FCSTD DOCUMENT  (FreeCAD 1.2R20251216 (Git shallow))
Label: gripper-assembly
License: All rights reserved
LicenseURL: https://en.wikipedia.org/wiki/All_rights_reserved
objects: App::FeaturePython×38, App::Link×31, App::DocumentObjectGroup×2, App::Point×1, Assembly::JointGroup×1, Assembly::AssemblyObject×1
EXTERNAL_REF file=gripper-parts.FCStd obj=Body077
EXTERNAL_REF file=gripper-parts.FCStd obj=Body076
EXTERNAL_REF file=gripper-parts.FCStd obj=Part__Mirroring004
EXTERNAL_REF file=gripper-parts.FCStd obj=Body059
EXTERNAL_REF file=gripper-parts.FCStd obj=Body058
EXTERNAL_REF file=gripper-parts.FCStd obj=Body057
EXTERNAL_REF file=gripper-parts.FCStd obj=Body056
EXTERNAL_REF file=gripper-parts.FCStd obj=Body055
EXTERNAL_REF file=gripper-parts.FCStd obj=Body054
EXTERNAL_REF file=gripper-parts.FCStd obj=Part015
EXTERNAL_REF file=gripper-parts.FCStd obj=Body050
EXTERNAL_REF file=gripper-parts.FCStd obj=Body044
EXTERNAL_REF file=gripper-parts.FCStd obj=Part__Mirroring
EXTERNAL_REF file=gripper-parts.FCStd obj=Body051
EXTERNAL_REF file=gripper-parts.FCStd obj=Body052
EXTERNAL_REF file=gripper-parts.FCStd obj=Body
EXTERNAL_REF file=gripper-parts.FCStd obj=Solid
EXTERNAL_REF file=gripper-parts.FCStd obj=Body002
EXTERNAL_REF file=gripper-parts.FCStd obj=Part__Mirroring003
EXTERNAL_REF file=gripper-parts.FCStd obj=Part__Mirroring002
EXTERNAL_REF file=gripper-parts.FCStd obj=Part__Mirroring005
EXTERNAL_REF file=gripper-parts.FCStd obj=Part__Mirroring006
EXTERNAL_REF file=gripper-parts.FCStd obj=Body081

FEATURE [App::Point] Origin001  label="Origine"
  Role = Origin
FEATURE [App::Link] Corps008
  LinkPlacement = pos=(-54,-64.2599,-158.309) rot=(1,0,0;0.193602rad)
  LinkedObject = -> <external gripper-parts.FCStd>#Body077
  Placement = pos=(-54,-64.2599,-158.309) rot=(1,0,0;0.193602rad)
FEATURE [App::Link] Corps007
  LinkPlacement = pos=(-54,-64.2599,-158.309) rot=(1,0,0;0.193602rad)
  LinkedObject = -> <external gripper-parts.FCStd>#Body076
  Placement = pos=(-54,-64.2599,-158.309) rot=(1,0,0;0.193602rad)
FEATURE [App::Link] Clone004__Mirror__5_  label="Clone004 (Mirror #5)"
  LinkPlacement = pos=(-74,-27.8311,-153.278) rot=(1,0,0;0.109071rad)
  LinkedObject = -> <external gripper-parts.FCStd>#Part__Mirroring004
  Placement = pos=(-74,-27.8311,-153.278) rot=(1,0,0;0.109071rad)
FEATURE [App::Link] SupportServoPivot
  LinkPlacement = pos=(-56.5,-64.2599,-158.309) rot=(1,0,0;0.193602rad)
  LinkedObject = -> <external gripper-parts.FCStd>#Body059
  Placement = pos=(-56.5,-64.2599,-158.309) rot=(1,0,0;0.193602rad)
FEATURE [App::Link] Corps005
  LinkPlacement = pos=(-38,-33.1693,-169.299) rot=(-1,0,0;0.353583rad)
  LinkedObject = -> <external gripper-parts.FCStd>#Body058
  Placement = pos=(-38,-33.1693,-169.299) rot=(-1,0,0;0.353583rad)
FEATURE [App::Link] Palonnier
  LinkPlacement = pos=(-38,-40.1387,-176.391) rot=(-1,0,0;0.252902rad)
  LinkedObject = -> <external gripper-parts.FCStd>#Body057
  Placement = pos=(-38,-40.1387,-176.391) rot=(-1,0,0;0.252902rad)
FEATURE [App::Link] Corps003
  LinkPlacement = pos=(-34,-43.7855,-150.498) rot=(1,0,0;0.166053rad)
  LinkedObject = -> <external gripper-parts.FCStd>#Body056
  Placement = pos=(-34,-43.7855,-150.498) rot=(1,0,0;0.166053rad)
FEATURE [App::Link] Corps002
  LinkPlacement = pos=(-34,-27.8311,-153.278) rot=(1,0,0;0.109071rad)
  LinkedObject = -> <external gripper-parts.FCStd>#Body055
  Placement = pos=(-34,-27.8311,-153.278) rot=(1,0,0;0.109071rad)
FEATURE [App::Link] SupportServoGripper
  LinkPlacement = pos=(-54,-18.1938,-168.324) rot=(-1,0,0;0.490525rad)
  LinkedObject = -> <external gripper-parts.FCStd>#Body054
  Placement = pos=(-54,-18.1938,-168.324) rot=(-1,0,0;0.490525rad)
FEATURE [App::Link] MG996
  LinkPlacement = pos=(-39.5,-92.0197,-220.472) rot=(0.590034,-0.551108,0.590034;4.14898rad)
  LinkedObject = -> <external gripper-parts.FCStd>#Part015
  Placement = pos=(-39.5,-92.0197,-220.472) rot=(0.590034,-0.551108,0.590034;4.14898rad)
FEATURE [App::FeaturePython] Joint001  label="Fixed001"  # Assembly joint (typed FeaturePython)
  Angle = 0
  AngleMax = 0
  AngleMin = 0
  Detach1 = false
  Detach2 = false
  Distance = 0
  Distance2 = 0
  EnableAngleMax = false
  EnableAngleMin = false
  EnableLengthMax = false
  EnableLengthMin = false
  JointType = 0 (Fixed)
  LengthMax = 0
  LengthMin = 0
  Placement1 = pos=(-2.5,-50.1695,-70.4616) rot=(-0.57735,0.57735,0.57735;4.18879rad)
  Placement2 = pos=(8,-17.5388,-77.1547) rot=(0,1,0;3.14159rad)
  Reference1 = -> Assembly [Corps007.Edge9,Corps007.Edge9]
  Reference2 = -> Assembly [SupportServoPivot.?Edge93,SupportServoPivot.?Edge93]
  Suppressed = false
FEATURE [App::FeaturePython] Joint003  label="Revolute003"  # Assembly joint (typed FeaturePython)
  Angle = 0
  AngleMax = 0
  AngleMin = 0
  Detach1 = false
  Detach2 = false
  Distance = 0
  Distance2 = 0
  EnableAngleMax = false
  EnableAngleMin = false
  EnableLengthMax = false
  EnableLengthMin = false
  JointType = 1 (Revolute)
  LengthMax = 0
  LengthMin = 0
  Placement1 = pos=(-53.5,-36.7417,-43.6373) rot=(-0.707107,0,0.707107;3.14159rad)
  Placement2 = pos=(12,-18.1231,-56.5257) rot=(0.707107,0,0.707107;3.14159rad)
  Reference1 = -> Assembly [Corps005.?Edge23,Corps005.?Edge23]
  Reference2 = -> Assembly [SupportServoPivot.?Edge142,SupportServoPivot.?Edge142]
  Suppressed = false
FEATURE [App::FeaturePython] Joint004  label="Revolute005"  # Assembly joint (typed FeaturePython)
  Angle = 0
  AngleMax = 0
  AngleMin = 0
  Detach1 = false
  Detach2 = false
  Distance = 0
  Distance2 = 0
  EnableAngleMax = false
  EnableAngleMin = false
  EnableLengthMax = false
  EnableLengthMin = false
  JointType = 1 (Revolute)
  LengthMax = 0
  LengthMin = 0
  Placement1 = pos=(-7.1e-15,-34.4956,-23.997) rot=(0.57735,0.57735,0.57735;2.0944rad)
  Placement2 = pos=(-34.0674,-41.631,2.88168) rot=(0.120076,-0.991913,0.041116;0.664795rad)
  Reference1 = -> Assembly [Corps003.Edge87,Corps003.Edge87]
  Reference2 = -> Assembly [Corps005.?Edge10,Corps005.?Edge10]
  Suppressed = false
FEATURE [App::FeaturePython] Joint005  label="Revolute006"  # Assembly joint (typed FeaturePython)
  Angle = 0
  AngleMax = 0
  AngleMin = 0
  Detach1 = false
  Detach2 = false
  Distance = 0
  Distance2 = 0
  EnableAngleMax = false
  EnableAngleMin = false
  EnableLengthMax = false
  EnableLengthMin = false
  JointType = 1 (Revolute)
  LengthMax = 0
  LengthMin = 0
  Placement1 = pos=(7.1e-15,-36.0964,7.29411) rot=(0.57735,0.57735,0.57735;2.0944rad)
  Placement2 = pos=(-17.8268,-39.1437,5.0239) rot=(0.260795,0.527251,0.808698;2.38057rad)
  Reference1 = -> Assembly [Corps002.Edge72,Corps002.Edge72]
  Reference2 = -> Assembly [Corps005.?Edge50,Corps005.?Edge50]
  Suppressed = false
FEATURE [App::FeaturePython] Joint009  label="Revolute008"  # Assembly joint (typed FeaturePython)
  Angle = 0
  AngleMax = 0
  AngleMin = 0
  Detach1 = false
  Detach2 = false
  Distance = 0
  Distance2 = 0
  EnableAngleMax = false
  EnableAngleMin = false
  EnableLengthMax = false
  EnableLengthMin = false
  JointType = 1 (Revolute)
  LengthMax = 0
  LengthMin = 0
  Placement1 = pos=(20,-10.5946,-40.1305) rot=(0.57735,0.57735,0.57735;2.0944rad)
  Placement2 = pos=(-7.1e-15,-10.5946,-47.1305) rot=(0.57735,0.57735,0.57735;2.0944rad)
  Reference1 = -> Assembly [SupportServoGripper.Edge136,SupportServoGripper.Edge136]
  Reference2 = -> Assembly [Corps003.Edge88,Corps003.Edge88]
  Suppressed = false
FEATURE [App::FeaturePython] Joint010  label="Revolute009"  # Assembly joint (typed FeaturePython)
  Angle = 0
  AngleMax = 0
  AngleMin = 0
  Detach1 = false
  Detach2 = false
  Distance = 0
  Distance2 = 0
  EnableAngleMax = false
  EnableAngleMin = false
  EnableLengthMax = false
  EnableLengthMin = false
  JointType = 1 (Revolute)
  LengthMax = 0
  LengthMin = 0
  Placement1 = pos=(20,-10.5946,-17.3494) rot=(0.57735,0.57735,0.57735;2.0944rad)
  Placement2 = pos=(0,-10.5946,-24.3494) rot=(0.57735,0.57735,0.57735;2.0944rad)
  Reference1 = -> Assembly [SupportServoGripper.Edge138,SupportServoGripper.Edge138]
  Reference2 = -> Assembly [Corps002.Edge71,Corps002.Edge71]
  Suppressed = false
FEATURE [App::FeaturePython] Joint013  label="Revolute012"  # Assembly joint (typed FeaturePython)
  Angle = 0
  AngleMax = 0
  AngleMin = 0
  Detach1 = false
  Detach2 = false
  Distance = 0
  Distance2 = 0
  EnableAngleMax = false
  EnableAngleMin = false
  EnableLengthMax = false
  EnableLengthMin = false
  JointType = 1 (Revolute)
  LengthMax = 0
  LengthMin = 0
  Placement1 = pos=(-20,-36.0964,7.29411) rot=(0.57735,0.57735,0.57735;2.0944rad)
  Placement2 = pos=(-26,-36.5317,-21.1945) rot=(0.707107,0,0.707107;3.14159rad)
  Reference1 = -> Assembly [Clone004__Mirror__5_.Edge72,Clone004__Mirror__5_.Edge72]
  Reference2 = -> Assembly [Corps005.?Edge131,Corps005.?Edge131]
  Suppressed = false
FEATURE [App::FeaturePython] Joint014  label="Revolute013"  # Assembly joint (typed FeaturePython)
  Angle = 0
  AngleMax = 0
  AngleMin = 0
  Detach1 = false
  Detach2 = false
  Distance = 0
  Distance2 = 0
  EnableAngleMax = false
  EnableAngleMin = false
  EnableLengthMax = false
  EnableLengthMin = false
  JointType = 1 (Revolute)
  LengthMax = 0
  LengthMin = 0
  Placement1 = pos=(-40,-10.5946,-17.3494) rot=(0.57735,0.57735,0.57735;2.0944rad)
  Placement2 = pos=(-20,-10.5946,-24.3494) rot=(0.57735,0.57735,0.57735;2.0944rad)
  Reference1 = -> Assembly [SupportServoGripper.Edge211,SupportServoGripper.Edge211]
  Reference2 = -> Assembly [Clone004__Mirror__5_.Edge71,Clone004__Mirror__5_.Edge71]
  Suppressed = false
FEATURE [App::Link] MG997
  LinkPlacement = pos=(-54,-17.8284,-146.412) rot=(-1,0,0;0.490525rad)
  LinkedObject = -> <external gripper-parts.FCStd>#Part015
  Placement = pos=(-54,-17.8284,-146.412) rot=(-1,0,0;0.490525rad)
FEATURE [App::Link] PalonnierDroit47mm
  LinkPlacement = pos=(-54,-17.1218,-145.089) rot=(-0.433241,-0.463484,0.772971;2.63327rad)
  LinkedObject = -> <external gripper-parts.FCStd>#Body050
  Placement = pos=(-54,-17.1218,-145.089) rot=(-0.433241,-0.463484,0.772971;2.63327rad)
FEATURE [App::FeaturePython] GroundedJoint  # Assembly grounded joint (typed FeaturePython)
  ObjectToGround = -> Corps007
FEATURE [App::FeaturePython] Joint  label="Fixed004"  # Assembly joint (typed FeaturePython)
  Angle = 0
  AngleMax = 0
  AngleMin = 0
  Detach1 = false
  Detach2 = false
  Distance = 0
  Distance2 = 0
  EnableAngleMax = false
  EnableAngleMin = false
  EnableLengthMax = false
  EnableLengthMin = false
  JointType = 0 (Fixed)
  LengthMax = 0
  LengthMin = 0
  Placement1 = pos=(14.5,5,-18.5) rot=(0,0,1;0rad)
  Placement2 = pos=(14.5,-5,-2.84e-14) rot=(0,0,1;0rad)
  Reference1 = -> Assembly [MG997.Body041.Edge63,MG997.Body041.Edge63]
  Reference2 = -> Assembly [SupportServoGripper.Edge33,SupportServoGripper.Edge33]
  Suppressed = false
FEATURE [App::FeaturePython] Joint015  label="Revolute014"  # Assembly joint (typed FeaturePython)
  Angle = 0
  AngleMax = 0
  AngleMin = 0
  Detach1 = false
  Detach2 = false
  Distance = 0
  Distance2 = 0
  EnableAngleMax = false
  EnableAngleMin = false
  EnableLengthMax = false
  EnableLengthMin = false
  JointType = 1 (Revolute)
  LengthMax = 0
  LengthMin = 0
  Placement1 = pos=(0,3.5,0) rot=(0,-0.707107,-0.707107;3.14159rad)
  Placement2 = pos=(0,0,-2) rot=(0,0,1;0rad)
  Reference1 = -> Assembly [PalonnierDroit47mm.Edge57,PalonnierDroit47mm.Edge57]
  Reference2 = -> Assembly [MG997.Body043.Edge5,MG997.Body043.Edge5]
  Suppressed = false
FEATURE [App::Link] FixationRailServoL
  LinkPlacement = pos=(-84,-14.8962,-162.149) rot=(0,0.242811,0.970074;3.14159rad)
  LinkedObject = -> <external gripper-parts.FCStd>#Body044
  Placement = pos=(-84,-14.8962,-162.149) rot=(0,0.242811,0.970074;3.14159rad)
FEATURE [App::Link] FixationRailServoR
  LinkPlacement = pos=(-54,-14.8962,-162.149) rot=(0,0.242811,0.970074;3.14159rad)
  LinkedObject = -> <external gripper-parts.FCStd>#Part__Mirroring
  Placement = pos=(-54,-14.8962,-162.149) rot=(0,0.242811,0.970074;3.14159rad)
FEATURE [App::FeaturePython] Joint016  label="Fixed006"  # Assembly joint (typed FeaturePython)
  Angle = 0
  AngleMax = 0
  AngleMin = 0
  Detach1 = false
  Detach2 = false
  Distance = 0
  Distance2 = 0
  EnableAngleMax = false
  EnableAngleMin = false
  EnableLengthMax = false
  EnableLengthMin = false
  JointType = 0 (Fixed)
  LengthMax = 0
  LengthMin = 0
  Offset2 = pos=(0,0,0) rot=(0,0,1;3.14159rad)
  Placement1 = pos=(4.5,5,-4.5) rot=(1,0,0;3.14159rad)
  Placement2 = pos=(-34.5,5,-16) rot=(0,0,1;3.14159rad)
  Reference1 = -> Assembly [FixationRailServoL.Edge40,FixationRailServoL.Edge40]
  Reference2 = -> Assembly [MG997.Body041.Edge38,MG997.Body041.Edge38]
  Suppressed = false
FEATURE [App::FeaturePython] Joint017  label="Fixed007"  # Assembly joint (typed FeaturePython)
  Angle = 0
  AngleMax = 0
  AngleMin = 0
  Detach1 = false
  Detach2 = false
  Distance = 0
  Distance2 = 0
  EnableAngleMax = false
  EnableAngleMin = false
  EnableLengthMax = false
  EnableLengthMin = false
  JointType = 0 (Fixed)
  LengthMax = 0
  LengthMin = 0
  Placement1 = pos=(-14.5,5,-4.5) rot=(0,0,-1;3.14159rad)
  Placement2 = pos=(14.5,5,-16) rot=(0,0,1;0rad)
  Reference1 = -> Assembly [FixationRailServoR.Edge40,FixationRailServoR.Edge40]
  Reference2 = -> Assembly [MG997.Body041.Edge52,MG997.Body041.Edge52]
  Suppressed = false
FEATURE [App::Link] CorpsRod
  LinkPlacement = pos=(-12.2755,-34.0056,-137.432) rot=(0.997269,-0.036328,-0.064299;2.53014rad)
  LinkedObject = -> <external gripper-parts.FCStd>#Body051
  Placement = pos=(-12.2755,-34.0056,-137.432) rot=(0.997269,-0.036328,-0.064299;2.53014rad)
FEATURE [App::Link] CorpsRod001
  LinkPlacement = pos=(-95.9284,1.64649,-149.217) rot=(0.029174,0.956629,-0.289846;3.20105rad)
  LinkedObject = -> <external gripper-parts.FCStd>#Body051
  Placement = pos=(-95.9284,1.64649,-149.217) rot=(0.029174,0.956629,-0.289846;3.20105rad)
FEATURE [App::Link] CorpsRod002
  LinkPlacement = pos=(-43.562,-30.757,-134.406) rot=(0.061354,0.301166,0.951596;3.07229rad)
  LinkedObject = -> <external gripper-parts.FCStd>#Body051
  Placement = pos=(-43.562,-30.757,-134.406) rot=(0.061354,0.301166,0.951596;3.07229rad)
FEATURE [App::Link] CorpsRod003
  LinkPlacement = pos=(-64.438,-0.659983,-150.48) rot=(-0.989829,0.101549,-0.099628;0.594088rad)
  LinkedObject = -> <external gripper-parts.FCStd>#Body051
  Placement = pos=(-64.438,-0.659983,-150.48) rot=(-0.989829,0.101549,-0.099628;0.594088rad)
FEATURE [App::Link] NoyauRod
  LinkPlacement = pos=(-12.2755,-34.0056,-137.432) rot=(-1,0,0;0.490525rad)
  LinkedObject = -> <external gripper-parts.FCStd>#Body052
  Placement = pos=(-12.2755,-34.0056,-137.432) rot=(-1,0,0;0.490525rad)
FEATURE [App::Link] NoyauRod001
  LinkPlacement = pos=(-95.9284,1.64649,-149.217) rot=(0,0.242811,0.970074;3.14159rad)
  LinkedObject = -> <external gripper-parts.FCStd>#Body052
  Placement = pos=(-95.9284,1.64649,-149.217) rot=(0,0.242811,0.970074;3.14159rad)
FEATURE [App::Link] NoyauRod002
  LinkPlacement = pos=(-64.438,-0.659983,-150.48) rot=(0.397515,0.222803,0.890135;5.15929rad)
  LinkedObject = -> <external gripper-parts.FCStd>#Body052
  Placement = pos=(-64.438,-0.659983,-150.48) rot=(0.397515,0.222803,0.890135;5.15929rad)
FEATURE [App::Link] NoyauRod003
  LinkPlacement = pos=(-43.562,-30.757,-134.406) rot=(0.13485,-0.240593,-0.961213;4.12992rad)
  LinkedObject = -> <external gripper-parts.FCStd>#Body052
  Placement = pos=(-43.562,-30.757,-134.406) rot=(0.13485,-0.240593,-0.961213;4.12992rad)
FEATURE [App::FeaturePython] Joint018  label="Fixed008"  # Assembly joint (typed FeaturePython)
  Angle = 0
  AngleMax = 0
  AngleMin = 0
  Detach1 = false
  Detach2 = false
  Distance = 0
  Distance2 = 0
  EnableAngleMax = false
  EnableAngleMin = false
  EnableLengthMax = false
  EnableLengthMin = false
  JointType = 0 (Fixed)
  LengthMax = 0
  LengthMin = 0
  Placement1 = pos=(0,0,-3) rot=(0,0,1;0rad)
  Placement2 = pos=(-20,-2.84e-14,7.1e-15) rot=(1,0,0;1.5708rad)
  Reference1 = -> Assembly [NoyauRod003.Edge8,NoyauRod003.Edge8]
  Reference2 = -> Assembly [PalonnierDroit47mm.Edge34,PalonnierDroit47mm.Edge34]
  Suppressed = false
FEATURE [App::FeaturePython] Joint019  label="Fixed009"  # Assembly joint (typed FeaturePython)
  Angle = 0
  AngleMax = 0
  AngleMin = 0
  Detach1 = false
  Detach2 = false
  Distance = 0
  Distance2 = 0
  EnableAngleMax = false
  EnableAngleMin = false
  EnableLengthMax = false
  EnableLengthMin = false
  JointType = 0 (Fixed)
  LengthMax = 0
  LengthMin = 0
  Placement1 = pos=(1.42e-14,7.1e-15,-3) rot=(0,0,1;0rad)
  Placement2 = pos=(20,2.84e-14,0) rot=(0,-0.707107,-0.707107;3.14159rad)
  Reference1 = -> Assembly [NoyauRod002.Edge8,NoyauRod002.Edge8]
  Reference2 = -> Assembly [PalonnierDroit47mm.Edge47,PalonnierDroit47mm.Edge47]
  Suppressed = false
FEATURE [App::FeaturePython] Joint020  label="Ball010"  # Assembly joint (typed FeaturePython)
  Angle = 0
  AngleMax = 0
  AngleMin = 0
  Detach1 = false
  Detach2 = false
  Distance = 0
  Distance2 = 0
  EnableAngleMax = false
  EnableAngleMin = false
  EnableLengthMax = false
  EnableLengthMin = false
  JointType = 4 (Ball)
  LengthMax = 0
  LengthMin = 0
  Placement1 = pos=(0,0,0) rot=(0,1,0;3.14159rad)
  Placement2 = pos=(0,0,0) rot=(0,0,-1;3.14159rad)
  Reference1 = -> Assembly [CorpsRod003.Face10,CorpsRod003.Face10]
  Reference2 = -> Assembly [NoyauRod002.Face1,NoyauRod002.Face1]
  Suppressed = false
FEATURE [App::FeaturePython] Joint021  label="Ball011"  # Assembly joint (typed FeaturePython)
  Angle = 0
  AngleMax = 0
  AngleMin = 0
  Detach1 = false
  Detach2 = false
  Distance = 0
  Distance2 = 0
  EnableAngleMax = false
  EnableAngleMin = false
  EnableLengthMax = false
  EnableLengthMin = false
  JointType = 4 (Ball)
  LengthMax = 0
  LengthMin = 0
  Placement1 = pos=(0,0,0) rot=(0,-1,0;3.14159rad)
  Placement2 = pos=(0,0,0) rot=(0,0,1;3.14159rad)
  Reference1 = -> Assembly [CorpsRod002.Face10,CorpsRod002.Face10]
  Reference2 = -> Assembly [NoyauRod003.Face1,NoyauRod003.Face1]
  Suppressed = false
FEATURE [App::FeaturePython] Joint022  label="Fixed010"  # Assembly joint (typed FeaturePython)
  Angle = 0
  AngleMax = 0
  AngleMin = 0
  Detach1 = false
  Detach2 = false
  Distance = 0
  Distance2 = 0
  EnableAngleMax = false
  EnableAngleMin = false
  EnableLengthMax = false
  EnableLengthMin = false
  JointType = 0 (Fixed)
  LengthMax = 0
  LengthMin = 0
  Placement1 = pos=(-15.8,0,0) rot=(0.57735,-0.57735,-0.57735;2.0944rad)
  Placement2 = pos=(-15.8,0,0) rot=(-0.57735,0.57735,0.57735;4.18879rad)
  Reference1 = -> Assembly [CorpsRod003.Edge25,CorpsRod003.Edge25]
  Reference2 = -> Assembly [CorpsRod001.Edge25,CorpsRod001.Edge25]
  Suppressed = false
FEATURE [App::FeaturePython] Joint023  label="Fixed012"  # Assembly joint (typed FeaturePython)
  Angle = 0
  AngleMax = 0
  AngleMin = 0
  Detach1 = false
  Detach2 = false
  Distance = 0
  Distance2 = 0
  EnableAngleMax = false
  EnableAngleMin = false
  EnableLengthMax = false
  EnableLengthMin = false
  JointType = 0 (Fixed)
  LengthMax = 0
  LengthMin = 0
  Placement1 = pos=(-15.8,2.13e-14,0) rot=(-0.57735,0.57735,0.57735;4.18879rad)
  Placement2 = pos=(-15.8,-7.1e-15,0) rot=(0.57735,-0.57735,-0.57735;2.0944rad)
  Reference1 = -> Assembly [CorpsRod.Edge25,CorpsRod.Edge25]
  Reference2 = -> Assembly [CorpsRod002.Edge25,CorpsRod002.Edge25]
  Suppressed = false
FEATURE [App::FeaturePython] Joint024  label="Ball013"  # Assembly joint (typed FeaturePython)
  Angle = 0
  AngleMax = 0
  AngleMin = 0
  Detach1 = false
  Detach2 = false
  Distance = 0
  Distance2 = 0
  EnableAngleMax = false
  EnableAngleMin = false
  EnableLengthMax = false
  EnableLengthMin = false
  JointType = 4 (Ball)
  LengthMax = 0
  LengthMin = 0
  Placement1 = pos=(0,0,0) rot=(0,0,-1;3.14159rad)
  Placement2 = pos=(0,0,0) rot=(0,-1,0;3.14159rad)
  Reference1 = -> Assembly [NoyauRod001.Face1,NoyauRod001.Face1]
  Reference2 = -> Assembly [CorpsRod001.Face10,CorpsRod001.Face10]
  Suppressed = false
FEATURE [App::FeaturePython] Joint025  label="Ball014"  # Assembly joint (typed FeaturePython)
  Angle = 0
  AngleMax = 0
  AngleMin = 0
  Detach1 = false
  Detach2 = false
  Distance = 0
  Distance2 = 0
  EnableAngleMax = false
  EnableAngleMin = false
  EnableLengthMax = false
  EnableLengthMin = false
  JointType = 4 (Ball)
  LengthMax = 0
  LengthMin = 0
  Placement1 = pos=(0,0,0) rot=(0,0,1;3.14159rad)
  Placement2 = pos=(0,0,0) rot=(0,1,0;3.14159rad)
  Reference1 = -> Assembly [NoyauRod.Face1,NoyauRod.Face1]
  Reference2 = -> Assembly [CorpsRod.Face10,CorpsRod.Face10]
  Suppressed = false
FEATURE [App::Link] Rail_MGN9___150mm  label="Rail MGN9 - 150mm"
  LinkPlacement = pos=(-54,-14.8962,-162.149) rot=(-1,0,0;0.490525rad)
  LinkedObject = -> <external gripper-parts.FCStd>#Body
  Placement = pos=(-54,-14.8962,-162.149) rot=(-1,0,0;0.490525rad)
FEATURE [App::FeaturePython] Joint026  label="Fixed014"  # Assembly joint (typed FeaturePython)
  Angle = 0
  AngleMax = 0
  AngleMin = 0
  Detach1 = false
  Detach2 = false
  Distance = 0
  Distance2 = 0
  EnableAngleMax = false
  EnableAngleMin = false
  EnableLengthMax = false
  EnableLengthMin = false
  JointType = 0 (Fixed)
  LengthMax = 0
  LengthMin = 0
  Placement1 = pos=(30,0,0) rot=(1,0,0;1.5708rad)
  Placement2 = pos=(-30,0,0) rot=(0,-0.707107,-0.707107;3.14159rad)
  Reference1 = -> Assembly [Rail_MGN9___150mm.Edge15,Rail_MGN9___150mm.Edge15]
  Reference2 = -> Assembly [FixationRailServoR.Edge24,FixationRailServoR.Edge24]
  Suppressed = false
FEATURE [App::Link] mgn9c
  LinkPlacement = pos=(-2.77549,-13.132,-163.091) rot=(-1,0,0;0.490525rad)
  LinkedObject = -> <external gripper-parts.FCStd>#Solid
  Placement = pos=(-2.77549,-13.132,-163.091) rot=(-1,0,0;0.490525rad)
FEATURE [App::Link] mgn9c001
  LinkPlacement = pos=(-105.428,-13.132,-163.091) rot=(-1,0,0;0.490525rad)
  LinkedObject = -> <external gripper-parts.FCStd>#Solid
  Placement = pos=(-105.428,-13.132,-163.091) rot=(-1,0,0;0.490525rad)
FEATURE [App::FeaturePython] Joint027  label="Slider016"  # Assembly joint (typed FeaturePython)
  Angle = 0
  AngleMax = 0
  AngleMin = 0
  Detach1 = false
  Detach2 = false
  Distance = 0
  Distance2 = 0
  EnableAngleMax = false
  EnableAngleMin = false
  EnableLengthMax = false
  EnableLengthMin = false
  JointType = 3 (Slider)
  LengthMax = 0
  LengthMin = 0
  Offset2 = pos=(0,0,0) rot=(0,0,1;3.14159rad)
  Placement1 = pos=(14.45,2.5,4.8) rot=(0,1,0;1.5708rad)
  Placement2 = pos=(100,4.5,4.8) rot=(-0.707107,0,0.707107;3.14159rad)
  Reference1 = -> Assembly [mgn9c.Edge11,mgn9c.Edge11]
  Reference2 = -> Assembly [Rail_MGN9___150mm.Edge69,Rail_MGN9___150mm.Edge69]
  Suppressed = false
FEATURE [App::FeaturePython] Joint028  label="Slider017"  # Assembly joint (typed FeaturePython)
  Angle = 0
  AngleMax = 0
  AngleMin = 0
  Detach1 = false
  Detach2 = false
  Distance = 0
  Distance2 = 0
  EnableAngleMax = false
  EnableAngleMin = false
  EnableLengthMax = false
  EnableLengthMin = false
  JointType = 3 (Slider)
  LengthMax = 0
  LengthMin = 0
  Placement1 = pos=(-14.45,2.5,4.8) rot=(0,1,0;1.5708rad)
  Placement2 = pos=(-100,4.5,4.8) rot=(-0.707107,0,0.707107;3.14159rad)
  Reference1 = -> Assembly [mgn9c001.Edge35,mgn9c001.Edge35]
  Reference2 = -> Assembly [Rail_MGN9___150mm.Edge51,Rail_MGN9___150mm.Edge51]
  Suppressed = false
FEATURE [App::Link] JawL
  LinkPlacement = pos=(-105.428,-6.0753,-166.86) rot=(-1,0,0;0.490525rad)
  LinkedObject = -> <external gripper-parts.FCStd>#Body002
  Placement = pos=(-105.428,-6.0753,-166.86) rot=(-1,0,0;0.490525rad)
FEATURE [App::Link] JawR
  LinkPlacement = pos=(-2.77549,-14.8962,-162.149) rot=(-1,0,0;0.490525rad)
  LinkedObject = -> <external gripper-parts.FCStd>#Part__Mirroring003
  Placement = pos=(-2.77549,-14.8962,-162.149) rot=(-1,0,0;0.490525rad)
FEATURE [App::Link] ExtensionJawR
  LinkPlacement = pos=(-42.7755,-15.0846,-162.502) rot=(-1,0,0;0.490525rad)
  LinkedObject = -> <external gripper-parts.FCStd>#Part__Mirroring002
  Placement = pos=(-42.7755,-15.0846,-162.502) rot=(-1,0,0;0.490525rad)
FEATURE [App::DocumentObjectGroup] Group001  label="Gripper"
  Group = -> [MG997,PalonnierDroit47mm,FixationRailServoL,FixationRailServoR,CorpsRod,CorpsRod001,CorpsRod002,CorpsRod003,NoyauRod,NoyauRod001,NoyauRod002,NoyauRod003,Rail_MGN9___150mm,mgn9c,mgn9c001,JawL,JawR,ExtensionJawR]
FEATURE [App::FeaturePython] Joint029  label="Fixed015"  # Assembly joint (typed FeaturePython)
  Angle = 0
  AngleMax = 0
  AngleMin = 0
  Detach1 = false
  Detach2 = false
  Distance = 0
  Distance2 = 0
  EnableAngleMax = false
  EnableAngleMin = false
  EnableLengthMax = false
  EnableLengthMin = false
  JointType = 0 (Fixed)
  LengthMax = 0
  LengthMin = 0
  Offset2 = pos=(0,0,0) rot=(0,0,-1;1.5708rad)
  Placement1 = pos=(-5,10,7.5) rot=(0,0.707107,0.707107;3.14159rad)
  Placement2 = pos=(-5,8,7.5) rot=(0,0.707107,0.707107;3.14159rad)
  Reference1 = -> Assembly [JawR.Edge117,JawR.Edge117]
  Reference2 = -> Assembly [mgn9c.Edge183,mgn9c.Edge183]
  Suppressed = false
FEATURE [App::FeaturePython] Joint030  label="Fixed016"  # Assembly joint (typed FeaturePython)
  Angle = 0
  AngleMax = 0
  AngleMin = 0
  Detach1 = false
  Detach2 = false
  Distance = 0
  Distance2 = 0
  EnableAngleMax = false
  EnableAngleMin = false
  EnableLengthMax = false
  EnableLengthMin = false
  JointType = 0 (Fixed)
  LengthMax = 0
  LengthMin = 0
  Offset2 = pos=(0,0,0) rot=(0,0,1;1.5708rad)
  Placement1 = pos=(5,0,7.5) rot=(1,0,0;1.5708rad)
  Placement2 = pos=(5,8,7.5) rot=(1,0,0;4.71239rad)
  Reference1 = -> Assembly [JawL.Edge117,JawL.Edge117]
  Reference2 = -> Assembly [mgn9c001.Edge186,mgn9c001.Edge186]
  Suppressed = false
FEATURE [App::FeaturePython] Joint031  label="Fixed017"  # Assembly joint (typed FeaturePython)
  Angle = 0
  AngleMax = 0
  AngleMin = 0
  Detach1 = false
  Detach2 = false
  Distance = 0
  Distance2 = 0
  EnableAngleMax = false
  EnableAngleMin = false
  EnableLengthMax = false
  EnableLengthMin = false
  JointType = 0 (Fixed)
  LengthMax = 0
  LengthMin = 0
  Offset2 = pos=(0,0,0) rot=(0,0,1;3.14159rad)
  Placement1 = pos=(30.5,8.5,16.6) rot=(0,1,0;3.14159rad)
  Placement2 = pos=(-9.5,8.5,16.2) rot=(0,-1,0;3.14159rad)
  Reference1 = -> Assembly [ExtensionJawR.Edge52,ExtensionJawR.Edge52]
  Reference2 = -> Assembly [JawR.Edge8,JawR.Edge8]
  Suppressed = false
FEATURE [App::FeaturePython] Joint032  label="Fixed018"  # Assembly joint (typed FeaturePython)
  Angle = 0
  AngleMax = 0
  AngleMin = 0
  Detach1 = false
  Detach2 = false
  Distance = 0
  Distance2 = 0
  EnableAngleMax = false
  EnableAngleMin = false
  EnableLengthMax = false
  EnableLengthMin = false
  JointType = 0 (Fixed)
  LengthMax = 0
  LengthMin = 0
  Placement1 = pos=(0,0,3) rot=(0,0,1;0rad)
  Placement2 = pos=(30.5,-28.5,16.2) rot=(0,1,0;3.14159rad)
  Reference1 = -> Assembly [NoyauRod.Edge10,NoyauRod.Edge10]
  Reference2 = -> Assembly [ExtensionJawR.Edge29,ExtensionJawR.Edge29]
  Suppressed = false
FEATURE [App::FeaturePython] Joint033  label="Fixed019"  # Assembly joint (typed FeaturePython)
  Angle = 0
  AngleMax = 0
  AngleMin = 0
  Detach1 = false
  Detach2 = false
  Distance = 0
  Distance2 = 0
  EnableAngleMax = false
  EnableAngleMin = false
  EnableLengthMax = false
  EnableLengthMin = false
  JointType = 0 (Fixed)
  LengthMax = 0
  LengthMin = 0
  Placement1 = pos=(0,1.42e-14,-3) rot=(0,0,1;0rad)
  Placement2 = pos=(9.5,-1.5,16.2) rot=(0,0,1;3.14159rad)
  Reference1 = -> Assembly [NoyauRod001.Edge11,NoyauRod001.Edge11]
  Reference2 = -> Assembly [JawL.Edge8,JawL.Edge8]
  Suppressed = false
FEATURE [App::FeaturePython] Joint034  label="Fixed"  # Assembly joint (typed FeaturePython)
  Angle = 0
  AngleMax = 0
  AngleMin = 0
  Detach1 = false
  Detach2 = false
  Distance = 0
  Distance2 = 0
  EnableAngleMax = false
  EnableAngleMin = false
  EnableLengthMax = false
  EnableLengthMin = false
  JointType = 0 (Fixed)
  LengthMax = 0
  LengthMin = 0
  Placement1 = pos=(-33.5,-50.1695,-70.4616) rot=(-0.57735,0.57735,0.57735;4.18879rad)
  Placement2 = pos=(-33.5,-50.1695,-70.4616) rot=(-0.57735,0.57735,0.57735;4.18879rad)
  Reference1 = -> Assembly [Corps008.Edge21,Corps008.Edge21]
  Reference2 = -> Assembly [Corps007.Edge32,Corps007.Edge32]
  Suppressed = false
FEATURE [App::Link] Body079__Mirror__6_  label="Body079 (Mirror #6)"
  LinkPlacement = pos=(-74,-43.7855,-150.498) rot=(1,0,0;0.166053rad)
  LinkedObject = -> <external gripper-parts.FCStd>#Part__Mirroring005
  Placement = pos=(-74,-43.7855,-150.498) rot=(1,0,0;0.166053rad)
FEATURE [App::DocumentObjectGroup] Group  label="PivotPrincipal"
  Group = -> [Corps008,Corps007,Clone004__Mirror__5_,SupportServoPivot,Corps005,Palonnier,Corps003,Corps002,SupportServoGripper,MG996,Body079__Mirror__6_]
FEATURE [App::FeaturePython] Joint035  label="Revolute020"  # Assembly joint (typed FeaturePython)
  Angle = 0
  AngleMax = 0
  AngleMin = 0
  Detach1 = false
  Detach2 = false
  Distance = 0
  Distance2 = 0
  EnableAngleMax = false
  EnableAngleMin = false
  EnableLengthMax = false
  EnableLengthMin = false
  JointType = 1 (Revolute)
  LengthMax = 0
  LengthMin = 0
  Placement1 = pos=(-20,-34.4956,-23.997) rot=(0.57735,0.57735,0.57735;2.0944rad)
  Placement2 = pos=(-52,-34.182,-26.9806) rot=(0.596473,0.596473,-0.537067;2.15587rad)
  Reference1 = -> Assembly [Body079__Mirror__6_.Edge87,Body079__Mirror__6_.Edge87]
  Reference2 = -> Assembly [Corps005.?Edge129,Corps005.?Edge129]
  Suppressed = false
FEATURE [App::FeaturePython] Joint036  label="Revolute021"  # Assembly joint (typed FeaturePython)
  Angle = 0
  AngleMax = 0
  AngleMin = 0
  Detach1 = false
  Detach2 = false
  Distance = 0
  Distance2 = 0
  EnableAngleMax = false
  EnableAngleMin = false
  EnableLengthMax = false
  EnableLengthMin = false
  JointType = 1 (Revolute)
  LengthMax = 0
  LengthMin = 0
  Placement1 = pos=(-20,-10.5946,-47.1305) rot=(0.57735,0.57735,0.57735;2.0944rad)
  Placement2 = pos=(-40,-10.5946,-40.1305) rot=(0.57735,0.57735,0.57735;2.0944rad)
  Reference1 = -> Assembly [Body079__Mirror__6_.Edge88,Body079__Mirror__6_.Edge88]
  Reference2 = -> Assembly [SupportServoGripper.Edge209,SupportServoGripper.Edge209]
  Suppressed = false
FEATURE [App::FeaturePython] Joint037  label="Fixed021"  # Assembly joint (typed FeaturePython)
  Angle = 0
  AngleMax = 0
  AngleMin = 0
  Detach1 = false
  Detach2 = false
  Distance = 0
  Distance2 = 0
  EnableAngleMax = false
  EnableAngleMin = false
  EnableLengthMax = false
  EnableLengthMin = false
  JointType = 0 (Fixed)
  LengthMax = 0
  LengthMin = 0
  Offset2 = pos=(0,0,0) rot=(0,0,1;0.261799rad)
  Placement1 = pos=(14.5,5,-16) rot=(0,0,1;0rad)
  Placement2 = pos=(-7.1e-15,-54.501,-56.7371) rot=(-0.519988,0.677661,0.519988;4.33274rad)
  Reference1 = -> Assembly [MG996.Body041.Edge52,MG996.Body041.Edge52]
  Reference2 = -> Assembly [SupportServoPivot.Edge63,SupportServoPivot.Edge63]
  Suppressed = false
FEATURE [App::FeaturePython] Joint038  label="Revolute024"  # Assembly joint (typed FeaturePython)
  Angle = 0
  AngleMax = 0
  AngleMin = 0
  Detach1 = false
  Detach2 = false
  Distance = 0
  Distance2 = 0
  EnableAngleMax = false
  EnableAngleMin = false
  EnableLengthMax = false
  EnableLengthMin = false
  JointType = 1 (Revolute)
  LengthMax = 0
  LengthMin = 0
  Placement1 = pos=(4,-61.8186,-11.463) rot=(0.57735,0.57735,0.57735;2.0944rad)
  Placement2 = pos=(0,-61.8186,-11.463) rot=(0.57735,0.57735,0.57735;2.0944rad)
  Reference1 = -> Assembly [Palonnier.Edge51,Palonnier.Edge51]
  Reference2 = -> Assembly [Corps003.Edge86,Corps003.Edge86]
  Suppressed = false
FEATURE [App::FeaturePython] Joint039  label="Cylindrical022"  # Assembly joint (typed FeaturePython)
  Angle = 0
  AngleMax = 0
  AngleMin = 0
  Detach1 = false
  Detach2 = false
  Distance = 0
  Distance2 = 0
  EnableAngleMax = false
  EnableAngleMin = false
  EnableLengthMax = false
  EnableLengthMin = false
  JointType = 2 (Cylindrical)
  LengthMax = 0
  LengthMin = 0
  Placement1 = pos=(-7.1e-15,-39.201,-55.6603) rot=(0.57735,0.57735,0.57735;2.0944rad)
  Placement2 = pos=(0,6e-15,-6) rot=(0,0,1;0rad)
  Reference1 = -> Assembly [Palonnier.Edge33,Palonnier.Edge33]
  Reference2 = -> Assembly [MG996.Body041.Face4,MG996.Body041.Edge1]
  Suppressed = false
FEATURE [App::Link] Body080__Mirror__7_  label="Body080 (Mirror #7)"
  LinkPlacement = pos=(-74,-40.1387,-176.391) rot=(-1,0,0;0.252902rad)
  LinkedObject = -> <external gripper-parts.FCStd>#Part__Mirroring006
  Placement = pos=(-74,-40.1387,-176.391) rot=(-1,0,0;0.252902rad)
FEATURE [App::Link] Corps010
  LinkPlacement = pos=(-54,-40.1387,-176.391) rot=(-1,0,0;0.252902rad)
  LinkedObject = -> <external gripper-parts.FCStd>#Body081
  Placement = pos=(-54,-40.1387,-176.391) rot=(-1,0,0;0.252902rad)
FEATURE [App::FeaturePython] Joint040  label="Fixed022"  # Assembly joint (typed FeaturePython)
  Angle = 0
  AngleMax = 0
  AngleMin = 0
  Detach1 = false
  Detach2 = false
  Distance = 0
  Distance2 = 0
  EnableAngleMax = false
  EnableAngleMin = false
  EnableLengthMax = false
  EnableLengthMin = false
  JointType = 0 (Fixed)
  LengthMax = 0
  LengthMin = 0
  Offset2 = pos=(0,0,0) rot=(0,0,1;3.14159rad)
  Placement1 = pos=(16,-56.5391,-24.1105) rot=(0.57735,-0.57735,-0.57735;2.0944rad)
  Placement2 = pos=(-7.1e-15,-56.5391,-24.1105) rot=(0.57735,-0.57735,0.57735;4.18879rad)
  Reference1 = -> Assembly [Corps010.Edge22,Corps010.Edge22]
  Reference2 = -> Assembly [Palonnier.Edge37,Palonnier.Edge37]
  Suppressed = false
FEATURE [App::FeaturePython] Joint041  label="Revolute025"  # Assembly joint (typed FeaturePython)
  Angle = 0
  AngleMax = 0
  AngleMin = 0
  Detach1 = false
  Detach2 = false
  Distance = 0
  Distance2 = 0
  EnableAngleMax = false
  EnableAngleMin = false
  EnableLengthMax = false
  EnableLengthMin = false
  JointType = 1 (Revolute)
  LengthMax = 0
  LengthMin = 0
  Placement1 = pos=(-20,-61.8186,-11.463) rot=(0.57735,0.57735,0.57735;2.0944rad)
  Placement2 = pos=(-20,-61.8186,-11.463) rot=(0.57735,0.57735,0.57735;2.0944rad)
  Reference1 = -> Assembly [Body080__Mirror__7_.Edge57,Body080__Mirror__7_.Edge57]
  Reference2 = -> Assembly [Body079__Mirror__6_.Edge86,Body079__Mirror__6_.Edge86]
  Suppressed = false
FEATURE [App::FeaturePython] Joint042  label="Revolute026"  # Assembly joint (typed FeaturePython)
  Angle = 0
  AngleMax = 0
  AngleMin = 0
  Detach1 = false
  Detach2 = false
  Distance = 0
  Distance2 = 0
  EnableAngleMax = false
  EnableAngleMin = false
  EnableLengthMax = false
  EnableLengthMin = false
  JointType = 1 (Revolute)
  LengthMax = 0
  LengthMin = 0
  Placement1 = pos=(-36,-39.201,-55.6603) rot=(-0.57735,0.57735,0.57735;4.18879rad)
  Placement2 = pos=(-16,-39.201,-55.6603) rot=(0.57735,0.57735,0.57735;2.0944rad)
  Reference1 = -> Assembly [Corps008.Edge77,Corps008.Edge77]
  Reference2 = -> Assembly [Body080__Mirror__7_.Edge49,Body080__Mirror__7_.Edge49]
  Suppressed = false
FEATURE [Assembly::JointGroup] Joints
  Group = -> [Joint001,Joint003,Joint004,Joint005,Joint009,Joint010,Joint013,Joint014,GroundedJoint,Joint,Joint015,Joint016,Joint017,Joint018,Joint019,Joint020,Joint021,Joint022,Joint023,Joint024,Joint025,Joint026,Joint027,Joint028,Joint029,Joint030,Joint031,Joint032,Joint033,Joint034,Joint035,Joint036,Joint037,Joint038,Joint039,Joint040,Joint041,Joint042]
FEATURE [Assembly::AssemblyObject] Assembly  label="GripperAssembly"
  Group = -> [Joints,Joint001,Joint003,Joint004,Joint005,Joint009,Joint010,Joint013,Joint014,Group,Corps008,Corps007,Clone004__Mirror__5_,SupportServoPivot,Corps005,Palonnier,Corps003,Corps002,SupportServoGripper,MG996,Group001,GroundedJoint,Joint,Joint015,Joint016,Joint017,MG997,PalonnierDroit47mm,FixationRailServoL,FixationRailServoR,Joint018,Joint019,Joint020,Joint021,Joint022,Joint023,Joint024,Joint025,+34 more]
  Origin = -> Origin
  Type = Assembly

RESOLVED EXTERNAL PARTS (link-assembly join: the EXTERNAL_REF files above that resolve inside this repo's crawl, each included once):
---- part gripper-parts.FCStd = doc fcstd_15e31927af7a (169545 chars; too large to inline — full recipe in that document) ----
